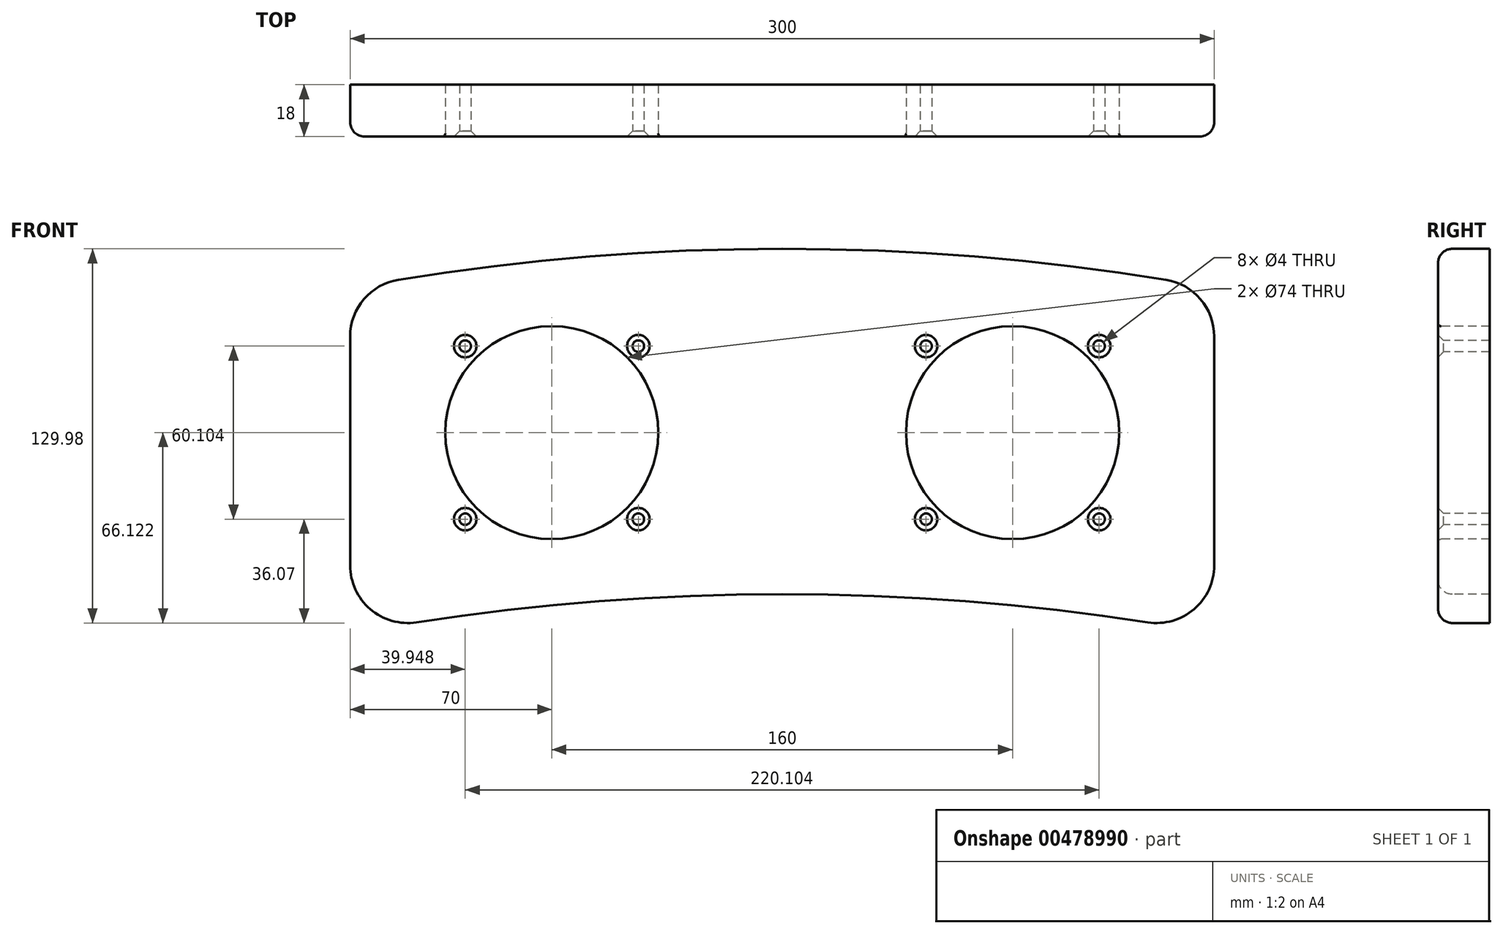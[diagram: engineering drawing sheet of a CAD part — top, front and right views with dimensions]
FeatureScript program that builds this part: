
annotation { "Feature Type Name" : "Feature", "Feature Type Description" : "" }
export const myFeature = defineFeature(function(context is Context, id is Id, definition is map)
    precondition{}
    {
        {
            var Q0;
            Q0=qCreatedBy(makeId("Front.planeOp"),FACE);
            var sketch = newSketch(context, id + "F0", { "sketchPlane" : qUnion([Q0])});
            skLineSegment(sketch, "E0", {"start": v(-80, 46.14) * mm, "end": v(80, 46.14) * mm, "construction": true});
            skLineSegment(sketch, "E1.bottom", {"start": v(-119, 7.14) * mm, "end": v(-41, 7.14) * mm, "construction": true});
            skLineSegment(sketch, "E1.top", {"start": v(-119, 85.14) * mm, "end": v(-41, 85.14) * mm, "construction": true});
            skLineSegment(sketch, "E1.left", {"start": v(-119, 7.14) * mm, "end": v(-119, 85.14) * mm, "construction": true});
            skLineSegment(sketch, "E1.right", {"start": v(-41, 7.14) * mm, "end": v(-41, 85.14) * mm, "construction": true});
            skPoint(sketch, "E1.middle", {"position": v(-80, 46.14) * mm});
            skLineSegment(sketch, "E2.bottom", {"start": v(119, 7.14) * mm, "end": v(41, 7.14) * mm, "construction": true});
            skLineSegment(sketch, "E2.top", {"start": v(119, 85.14) * mm, "end": v(41, 85.14) * mm, "construction": true});
            skLineSegment(sketch, "E2.left", {"start": v(119, 7.14) * mm, "end": v(119, 85.14) * mm, "construction": true});
            skLineSegment(sketch, "E2.right", {"start": v(41, 7.14) * mm, "end": v(41, 85.14) * mm, "construction": true});
            skPoint(sketch, "E2.middle", {"position": v(80, 46.14) * mm});
            skCircle(sketch, "E3", {"center": v(-80, 46.14) * mm, "radius": 37 * mm});
            skCircle(sketch, "E4", {"center": v(80, 46.14) * mm, "radius": 37 * mm});
            skLineSegment(sketch, "E5", {"start": v(-150, 79.52) * mm, "end": v(-150, 0.02) * mm});
            skLineSegment(sketch, "E6", {"start": v(0, 110) * mm, "end": v(0, -10) * mm, "construction": true});
            skLineSegment(sketch, "E7", {"start": v(150, 79.52) * mm, "end": v(150, 0.02) * mm});
            skPoint(sketch, "E8", {"position": v(-150, 36.36) * mm});
            skPoint(sketch, "E9", {"position": v(150, 36.36) * mm});
            skPoint(sketch, "E10", {"position": v(0, 50) * mm});
            skArc(sketch, "E11", {"start": v(133.2, 99.26) * mm, "mid": v(0, 110) * mm, "end": v(-133.2, 99.26) * mm});
            skArc(sketch, "E12", {"start": v(150, 36.36) * mm, "mid": v(0, 50) * mm, "end": v(-150, 36.36) * mm, "construction": true});
            skArc(sketch, "E13", {"start": v(126.95, -19.75) * mm, "mid": v(0, -10) * mm, "end": v(-126.95, -19.75) * mm});
            skPoint(sketch, "E14.visualSharp", {"position": v(-150, 96.36) * mm});
            skArc(sketch, "E14.filletArc", {"start": v(-133.2, 99.26) * mm, "mid": v(-145.23, 92.48) * mm, "end": v(-150, 79.52) * mm});
            skPoint(sketch, "E15.visualSharp", {"position": v(150, 96.36) * mm});
            skArc(sketch, "E15.filletArc", {"start": v(150, 79.52) * mm, "mid": v(145.23, 92.48) * mm, "end": v(133.2, 99.26) * mm});
            skPoint(sketch, "E16.visualSharp", {"position": v(150, -23.64) * mm});
            skArc(sketch, "E16.filletArc", {"start": v(126.95, -19.75) * mm, "mid": v(143.02, -15.17) * mm, "end": v(150, 0.02) * mm});
            skPoint(sketch, "E17.visualSharp", {"position": v(-150, -23.64) * mm});
            skArc(sketch, "E17.filletArc", {"start": v(-150, 0.02) * mm, "mid": v(-143.02, -15.17) * mm, "end": v(-126.95, -19.75) * mm});
            skLineSegment(sketch, "E18", {"start": v(-119, 85.14) * mm, "end": v(-41, 7.14) * mm, "construction": true});
            skLineSegment(sketch, "E19", {"start": v(-41, 85.14) * mm, "end": v(-119, 7.14) * mm, "construction": true});
            skLineSegment(sketch, "E20", {"start": v(41, 85.14) * mm, "end": v(119, 7.14) * mm, "construction": true});
            skLineSegment(sketch, "E21", {"start": v(119, 85.14) * mm, "end": v(41, 7.14) * mm, "construction": true});
            skCircle(sketch, "E22", {"center": v(-80, 46.14) * mm, "radius": 42.5 * mm, "construction": true});
            skCircle(sketch, "E23", {"center": v(80, 46.14) * mm, "radius": 42.5 * mm, "construction": true});
            skCircle(sketch, "E24", {"center": v(-49.95, 76.2) * mm, "radius": 2 * mm});
            skCircle(sketch, "E25", {"center": v(-110.05, 76.2) * mm, "radius": 2 * mm});
            skCircle(sketch, "E26", {"center": v(-110.05, 16.09) * mm, "radius": 2 * mm});
            skCircle(sketch, "E27", {"center": v(-49.95, 16.09) * mm, "radius": 2 * mm});
            skCircle(sketch, "E28", {"center": v(49.95, 76.2) * mm, "radius": 2 * mm});
            skCircle(sketch, "E29", {"center": v(49.95, 16.09) * mm, "radius": 2 * mm});
            skCircle(sketch, "E30", {"center": v(110.05, 76.2) * mm, "radius": 2 * mm});
            skCircle(sketch, "E31", {"center": v(110.05, 16.09) * mm, "radius": 2 * mm});
            skSolve(sketch);
        }
        {
            var Q0;
            Q0 = qSketchRegion(id + "F0", true);
            extrude(context, id + "F1", {"entities" : qUnion([Q0]), "oppositeDirection" : true, "depth" : 18 * mm});
        }
        {
            var Q0;
            Q0=makeQuery(id+"F1.opExtrude","CAP_EDGE",EDGE,{"disambiguationData":[OSD([sQuery(id+"F0.wireOp",EDGE,"E3")])],"isStart":true});
            var Q1;
            Q1=makeQuery(id+"F1.opExtrude","CAP_EDGE",EDGE,{"disambiguationData":[OSD([sQuery(id+"F0.wireOp",EDGE,"E4")])],"isStart":true});
            fillet(context, id + "F2", {"entities" : qUnion([Q0, Q1]), "radius" : 1 * mm, "tangentPropagation" : true, "allowEdgeOverflow" : false});
        }
        {
            var Q0;
            Q0=makeQuery(id+"F1.opExtrude","CAP_EDGE",EDGE,{"disambiguationData":[OSD([sQuery(id+"F0.wireOp",EDGE,"E11")])],"isStart":true});
            var Q1;
            Q1=makeQuery(id+"F1.opExtrude","CAP_EDGE",EDGE,{"disambiguationData":[OSD([sQuery(id+"F0.wireOp",EDGE,"E15.filletArc")])],"isStart":true});
            var Q2;
            Q2=makeQuery(id+"F1.opExtrude","CAP_EDGE",EDGE,{"disambiguationData":[OSD([sQuery(id+"F0.wireOp",EDGE,"E7")])],"isStart":true});
            var Q3;
            Q3=makeQuery(id+"F1.opExtrude","CAP_EDGE",EDGE,{"disambiguationData":[OSD([sQuery(id+"F0.wireOp",EDGE,"E16.filletArc")])],"isStart":true});
            var Q4;
            Q4=makeQuery(id+"F1.opExtrude","CAP_EDGE",EDGE,{"disambiguationData":[OSD([sQuery(id+"F0.wireOp",EDGE,"E13")])],"isStart":true});
            var Q5;
            Q5=makeQuery(id+"F1.opExtrude","CAP_EDGE",EDGE,{"disambiguationData":[OSD([sQuery(id+"F0.wireOp",EDGE,"E17.filletArc")])],"isStart":true});
            var Q6;
            Q6=makeQuery(id+"F1.opExtrude","CAP_EDGE",EDGE,{"disambiguationData":[OSD([sQuery(id+"F0.wireOp",EDGE,"E5")])],"isStart":true});
            var Q7;
            Q7=makeQuery(id+"F1.opExtrude","CAP_EDGE",EDGE,{"disambiguationData":[OSD([sQuery(id+"F0.wireOp",EDGE,"E14.filletArc")])],"isStart":true});
            fillet(context, id + "F3", {"entities" : qUnion([Q0, Q1, Q2, Q3, Q4, Q5, Q6, Q7]), "radius" : 5 * mm, "tangentPropagation" : true, "allowEdgeOverflow" : false});
        }
        {
            var Q0;
            Q0=makeQuery(id+"F1.opExtrude","CAP_EDGE",EDGE,{"disambiguationData":[OSD([sQuery(id+"F0.wireOp",EDGE,"E25")])],"isStart":true});
            var Q1;
            Q1=makeQuery(id+"F1.opExtrude","CAP_EDGE",EDGE,{"disambiguationData":[OSD([sQuery(id+"F0.wireOp",EDGE,"E24")])],"isStart":true});
            var Q2;
            Q2=makeQuery(id+"F1.opExtrude","CAP_EDGE",EDGE,{"disambiguationData":[OSD([sQuery(id+"F0.wireOp",EDGE,"E26")])],"isStart":true});
            var Q3;
            Q3=makeQuery(id+"F1.opExtrude","CAP_EDGE",EDGE,{"disambiguationData":[OSD([sQuery(id+"F0.wireOp",EDGE,"E27")])],"isStart":true});
            var Q4;
            Q4=makeQuery(id+"F1.opExtrude","CAP_EDGE",EDGE,{"disambiguationData":[OSD([sQuery(id+"F0.wireOp",EDGE,"E29")])],"isStart":true});
            var Q5;
            Q5=makeQuery(id+"F1.opExtrude","CAP_EDGE",EDGE,{"disambiguationData":[OSD([sQuery(id+"F0.wireOp",EDGE,"E28")])],"isStart":true});
            var Q6;
            Q6=makeQuery(id+"F1.opExtrude","CAP_EDGE",EDGE,{"disambiguationData":[OSD([sQuery(id+"F0.wireOp",EDGE,"E31")])],"isStart":true});
            var Q7;
            Q7=makeQuery(id+"F1.opExtrude","CAP_EDGE",EDGE,{"disambiguationData":[OSD([sQuery(id+"F0.wireOp",EDGE,"E30")])],"isStart":true});
            chamfer(context, id + "F4", {"entities" : qUnion([Q0, Q1, Q2, Q3, Q4, Q5, Q6, Q7]), "width" : 1.9 * mm, "tangentPropagation" : true});
        }
    });
